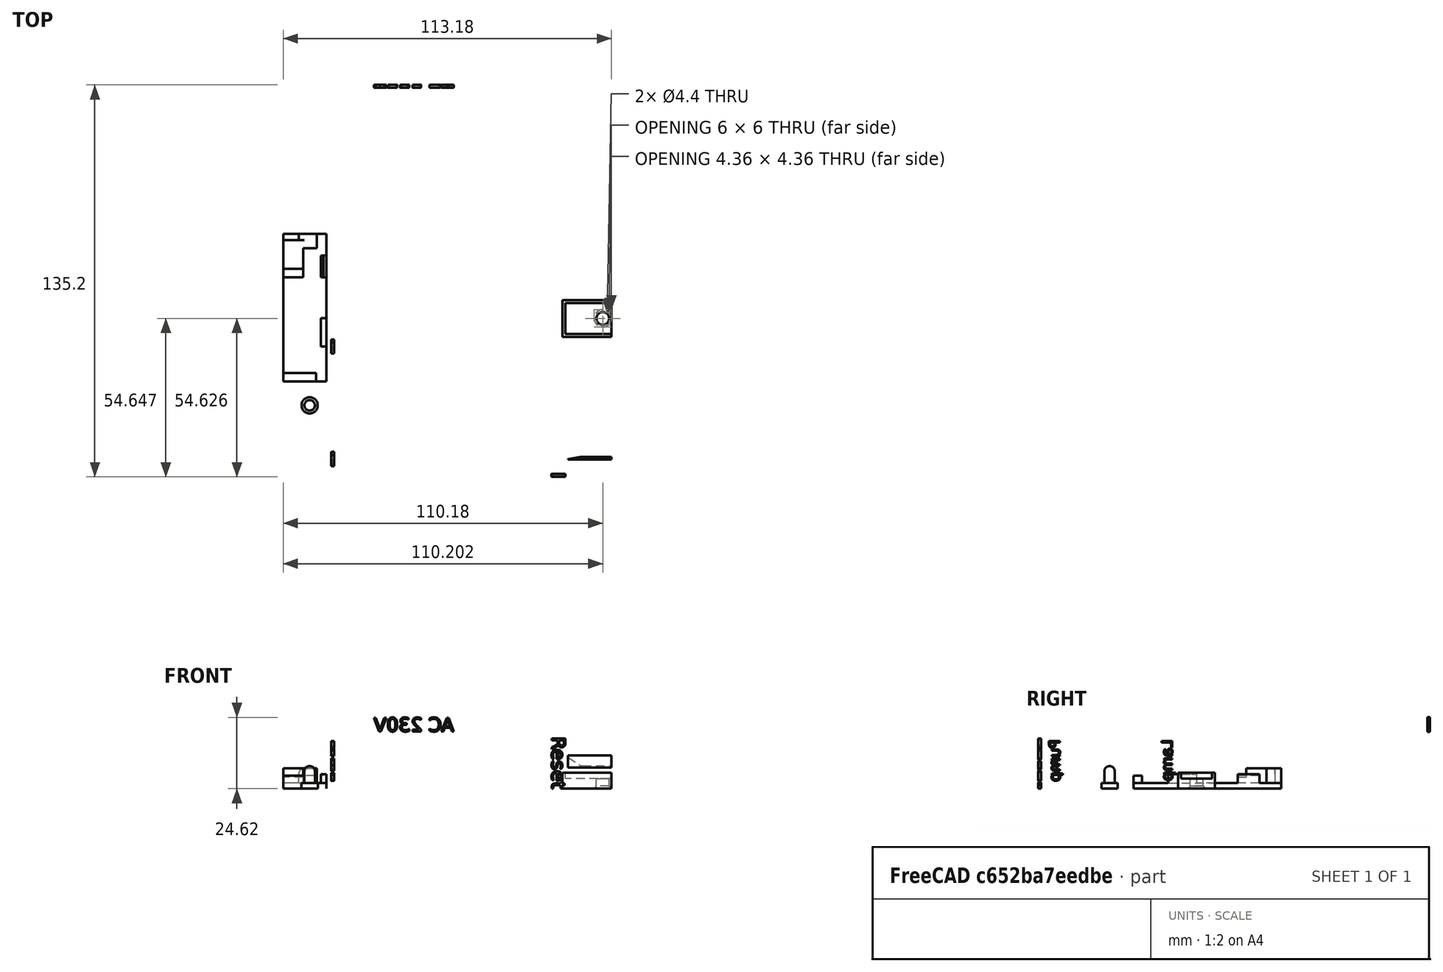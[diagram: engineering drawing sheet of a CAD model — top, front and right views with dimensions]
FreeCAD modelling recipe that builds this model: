
FCSTD DOCUMENT  (FreeCAD 0.21R33771 (Git))
Label: station.lamp.pump.100W
License: All rights reserved
LicenseURL: http://en.wikipedia.org/wiki/All_rights_reserved
objects: Part::FeaturePython×17, Part::Part2DObjectPython×7, Part::MultiFuse×5, App::DocumentObjectGroup×5, Part::Feature×3, Part::Refine×2, Part::Extrusion×1, Part::Cut×1
note: 36 computed .brp shape members not serialized (recipe doc carries the construction recipe); baked Part::Feature solids carry a one-line shape summary decoded from their .brp

FEATURE [Part::Part2DObjectPython] Rectangle  # Draft 2D object (typed FeaturePython)
  ChamferSize = 0
  Columns = 1
  FilletRadius = 0
  Height = 74.0625
  Length = 50.4262
  MakeFace = true
  Placement = pos=(152.909,-168.503,-194.387) rot=(1,0,0;1.5708rad)
  Rows = 1
FEATURE [Part::FeaturePython] Slice001_child2  label="Slice001.2"  # WARN: FeaturePython — macro-defined, semantics opaque (R4)
  FilterType = 1
  Invert = false
  OverrideMaxVal = 0
  WindowFrom = 80
  WindowTo = 100
  items = 2
FEATURE [Part::FeaturePython] Slice001_child3  label="Slice001.3"  # WARN: FeaturePython — macro-defined, semantics opaque (R4)
  FilterType = 1
  Invert = false
  OverrideMaxVal = 0
  WindowFrom = 80
  WindowTo = 100
  items = 3
FEATURE [Part::MultiFuse] Fusion005002002014004003003002009002010004002003006003008008004007002004008002005011019002002002007  label="Text"
FEATURE [Part::Feature] Fusion005002002014004003003002009002010004002003006003008008004007002004008002005001  label="Fusion005002002014004003003002009002010004002003006003008008004007002004008002006"
  shape: bbox 14.8 x 50.9 x 7 mm, 30 faces (baked)
FEATURE [Part::MultiFuse] Fusion005002002014004003003002009002010004002003006003008008004007002004008002003
  Placement = pos=(371.865,-232.312,-185.367) rot=(0,0,1;0rad)
FEATURE [Part::FeaturePython] Slice001_child4  label="Slice001.4"  # WARN: FeaturePython — macro-defined, semantics opaque (R4)
  FilterType = 1
  Invert = false
  OverrideMaxVal = 0
  WindowFrom = 80
  WindowTo = 100
  items = 4
FEATURE [Part::MultiFuse] Fusion005002002014004003003002009002010004002003006003008008004007002004008002005011019002002002012002
FEATURE [Part::FeaturePython] Slice  # WARN: FeaturePython — macro-defined, semantics opaque (R4)
  Base = -> Fusion005002002014004003003002009002010004002003006003008008004007002004008002005011019002002002012002
  Mode = 1
  Tolerance = 0
  Tools = -> [Rectangle]
FEATURE [Part::FeaturePython] Slice_child1  label="Slice.1"  # WARN: FeaturePython — macro-defined, semantics opaque (R4)
  Base = -> Slice
  FilterType = 1
  Invert = false
  OverrideMaxVal = 0
  WindowFrom = 80
  WindowTo = 100
  items = 1
FEATURE [Part::FeaturePython] Slice_child2  label="Slice.2"  # WARN: FeaturePython — macro-defined, semantics opaque (R4)
  Base = -> Slice
  FilterType = 1
  Invert = false
  OverrideMaxVal = 0
  WindowFrom = 80
  WindowTo = 100
  items = 2
FEATURE [Part::FeaturePython] Slice001_child5  label="Slice001.5"  # WARN: FeaturePython — macro-defined, semantics opaque (R4)
  FilterType = 1
  Invert = false
  OverrideMaxVal = 0
  WindowFrom = 80
  WindowTo = 100
  items = 5
FEATURE [Part::FeaturePython] Slice001_child1  label="Slice001.1"  # WARN: FeaturePython — macro-defined, semantics opaque (R4)
  FilterType = 1
  Invert = false
  OverrideMaxVal = 0
  WindowFrom = 80
  WindowTo = 100
  items = 1
FEATURE [Part::MultiFuse] Fusion
  Shapes = -> [Slice001_child3,Slice001_child2,Slice001_child5,Slice001_child4,Slice_child1,Slice001_child1]
FEATURE [Part::MultiFuse] Fusion005002002014004003003002009002010004002003006003008008004007002004008002005011019002002002012003  label="Text001"
  Shapes = -> [Fusion,Fusion005002002014004003003002009002010004002003006003008008004007002004008002005011019002002002007]
FEATURE [Part::FeaturePython] Slice_child0  label="Slice.0"  # WARN: FeaturePython — macro-defined, semantics opaque (R4)
  Base = -> Slice
  FilterType = 1
  Invert = false
  OverrideMaxVal = 0
  WindowFrom = 80
  WindowTo = 100
  items = 0
FEATURE [App::DocumentObjectGroup] GrExplode_Slice  label="Base"
  Group = -> [Slice_child0,Slice_child2]
FEATURE [Part::Part2DObjectPython] Line  # Draft 2D object (typed FeaturePython)
  Area = 0
  ChamferSize = 0
  Closed = false
  End = (79.4504,-136.503,-128.13)
  FilletRadius = 0
  Length = 53.8703
  MakeFace = true
  Placement = pos=(79.4504,-136.503,-182.001) rot=(0.57735,-0.57735,-0.57735;2.0944rad)
  Points = (2) [(0,0,0),(0,53.8703,0)]
  Start = (79.4504,-136.503,-182.001)
  Subdivisions = 0
FEATURE [Part::Part2DObjectPython] Circle  # Draft 2D object (typed FeaturePython)
  Area = 105.683
  FirstAngle = 0
  LastAngle = 0
  MakeFace = true
  Placement = pos=(79.4504,-136.503,-182.001) rot=(0.57735,-0.57735,-0.57735;2.0944rad)
  Radius = 5.8
FEATURE [Part::Part2DObjectPython] Rectangle002  # Draft 2D object (typed FeaturePython)
  Area = 51979.7
  ChamferSize = 0
  Columns = 1
  FilletRadius = 0
  Height = 192.992
  Length = 269.335
  MakeFace = true
  Placement = pos=(231.566,-108.503,-293.923) rot=(0,0.707107,0.707107;3.14159rad)
  Rows = 1
FEATURE [Part::FeaturePython] Slice001  # WARN: FeaturePython — macro-defined, semantics opaque (R4)
  Base = -> Slice_child0
  Mode = 1
  Tolerance = 0
  Tools = -> [Rectangle002]
FEATURE [Part::FeaturePython] Slice001_child0  label="Slice001.0"  # WARN: FeaturePython — macro-defined, semantics opaque (R4)
  Base = -> Slice001
  FilterType = 1
  Invert = false
  OverrideMaxVal = 0
  WindowFrom = 80
  WindowTo = 100
  items = 0
FEATURE [App::DocumentObjectGroup] GrExplode_Slice001  label="Exploded Slice001"
  Group = -> [Slice001_child0]
FEATURE [Part::Part2DObjectPython] Rectangle003  # Draft 2D object (typed FeaturePython)
  Area = 19823.8
  ChamferSize = 0
  Columns = 1
  FilletRadius = 0
  Height = 132.354
  Length = 149.778
  MakeFace = true
  Placement = pos=(52.2252,-132.903,-277.111) rot=(1,0,0;1.5708rad)
  Rows = 1
FEATURE [Part::FeaturePython] Slice002  # WARN: FeaturePython — macro-defined, semantics opaque (R4)
  Base = -> Slice001_child0
  Mode = 1
  Tolerance = 0
  Tools = -> [Rectangle003]
FEATURE [Part::FeaturePython] Slice002_child1  label="Slice002.1"  # WARN: FeaturePython — macro-defined, semantics opaque (R4)
  Base = -> Slice002
  FilterType = 1
  Invert = false
  OverrideMaxVal = 0
  WindowFrom = 80
  WindowTo = 100
  items = 1
FEATURE [App::DocumentObjectGroup] GrExplode_Slice002  label="Exploded Slice002"
  Group = -> [Slice002_child1]
FEATURE [Part::Part2DObjectPython] Rectangle004  # Draft 2D object (typed FeaturePython)
  Area = 2274.63
  ChamferSize = 0
  Columns = 1
  FilletRadius = 0
  Height = 38.5992
  Length = 58.9295
  MakeFace = true
  Placement = pos=(158.22,-92.7159,-212.367) rot=(-0.57735,0.57735,0.57735;4.18879rad)
  Rows = 1
FEATURE [Part::FeaturePython] Slice003  # WARN: FeaturePython — macro-defined, semantics opaque (R4)
  Base = -> Slice002_child1
  Mode = 1
  Tolerance = 0
  Tools = -> [Rectangle004]
FEATURE [Part::FeaturePython] Slice003_child0  label="Slice003.0"  # WARN: FeaturePython — macro-defined, semantics opaque (R4)
  Base = -> Slice003
  FilterType = 1
  Invert = false
  OverrideMaxVal = 0
  WindowFrom = 80
  WindowTo = 100
  items = 0
FEATURE [App::DocumentObjectGroup] GrExplode_Slice003  label="Exploded Slice003"
  Group = -> [Slice003_child0]
FEATURE [Part::Part2DObjectPython] Rectangle005  # Draft 2D object (typed FeaturePython)
  Area = 1671.48
  ChamferSize = 0
  Columns = 1
  FilletRadius = 0
  Height = 47.293
  Length = 35.3431
  MakeFace = true
  Placement = pos=(150.565,-121.203,-222.32) rot=(1,0,0;1.5708rad)
  Rows = 1
FEATURE [Part::FeaturePython] Slice004  # WARN: FeaturePython — macro-defined, semantics opaque (R4)
  Base = -> Slice003_child0
  Mode = 1
  Tolerance = 0
  Tools = -> [Rectangle005]
FEATURE [Part::FeaturePython] Slice004_child0  label="Slice004.0"  # WARN: FeaturePython — macro-defined, semantics opaque (R4)
  Base = -> Slice004
  FilterType = 1
  Invert = false
  OverrideMaxVal = 0
  WindowFrom = 80
  WindowTo = 100
  items = 0
FEATURE [App::DocumentObjectGroup] GrExplode_Slice004  label="Exploded Slice004"
  Group = -> [Slice004_child0]
FEATURE [Part::Refine] Slice004_child001  label="Slice004.001"
  Source = -> Slice004_child0
FEATURE [Part::Feature] Face
  shape: bbox 9.5e-05 x 12.7 x 2 mm, 1 faces, 0 solids (baked)
FEATURE [Part::Extrusion] Extrusion
  Base = -> Face
  Dir = (-1.73,-1.39396e-11,8.07099e-11)
  DirMode = 0
  FaceMakerClass = Part::FaceMakerBullseye
  LengthFwd = 0
  LengthRev = 0
  Solid = true
  Symmetric = false
FEATURE [Part::Cut] Cut
  Base = -> Slice004_child001
  Tool = -> Extrusion
FEATURE [Part::Feature] Cut_solid  label="Cut (Solid)"
  shape: bbox 16.9 x 12.7 x 5.5 mm, 13 faces (baked)
FEATURE [Part::Refine] Cut001
  Source = -> Cut
